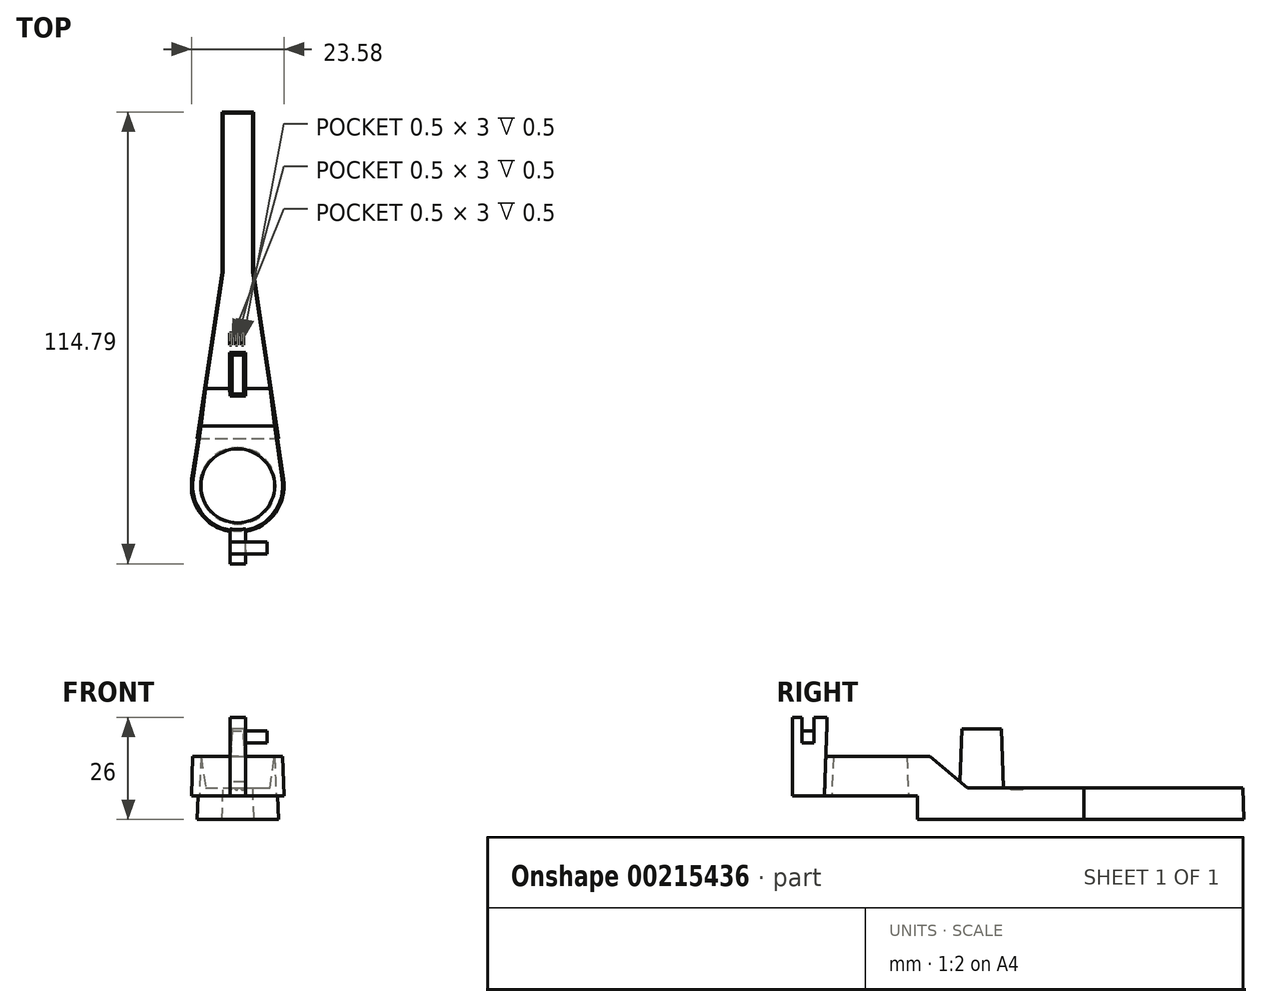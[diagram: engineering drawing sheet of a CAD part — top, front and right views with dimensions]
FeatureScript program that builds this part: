
annotation { "Feature Type Name" : "Feature", "Feature Type Description" : "" }
export const myFeature = defineFeature(function(context is Context, id is Id, definition is map)
    precondition{}
    {
        {
            var Q0;
            Q0=qCreatedBy(makeId("Top.planeOp"),FACE);
            var sketch = newSketch(context, id + "F0", { "sketchPlane" : qUnion([Q0])});
            skCircle(sketch, "E0", {"center": v(0, 0) * mm, "radius": 12 * mm});
            skLineSegment(sketch, "E1", {"start": v(-3, 95) * mm, "end": v(3, 95) * mm});
            skLineSegment(sketch, "E2", {"start": v(0, -12) * mm, "end": v(0, 95) * mm, "construction": true});
            skPoint(sketch, "E3", {"position": v(0, 95) * mm});
            skLineSegment(sketch, "E4", {"start": v(-4, 54.32) * mm, "end": v(-11.87, 1.78) * mm});
            skLineSegment(sketch, "E5", {"start": v(4, 54.32) * mm, "end": v(11.87, 1.78) * mm});
            skLineSegment(sketch, "E6", {"start": v(-3, 95) * mm, "end": v(-4, 95) * mm});
            skLineSegment(sketch, "E7", {"start": v(-4, 95) * mm, "end": v(-4, 54.32) * mm});
            skLineSegment(sketch, "E8", {"start": v(3, 95) * mm, "end": v(4, 95) * mm});
            skLineSegment(sketch, "E9", {"start": v(4, 95) * mm, "end": v(4, 54.32) * mm});
            skPoint(sketch, "E10.orphan", {"position": v(-3, 61) * mm});
            skPoint(sketch, "E11.orphan", {"position": v(3, 61) * mm});
            skSolve(sketch);
        }
        {
            var Q0;
            Q0=qSketchRegion(id+"F0",true);
            extrude(context, id + "F1", {"entities" : qUnion([Q0]), "depth" : 16 * mm, "hasDraft" : true, "draftAngle" : 2 * degree, "draftPullDirection" : true});
        }
        {
            var Q0;
            Q0=qCreatedBy(makeId("Right.planeOp"),FACE);
            cPlane(context, id + "F2", {"entities" : qUnion([Q0]), "cplaneType" : CPlaneType.OFFSET, "offset" : 12 * mm, "width" : 150 * mm, "height" : 150 * mm});
        }
        {
            var Q0;
            Q0=qCreatedBy(id+"F2.planeOp",FACE);
            var sketch = newSketch(context, id + "F3", { "sketchPlane" : qUnion([Q0])});
            skLineSegment(sketch, "E12", {"start": v(94.72, 8) * mm, "end": v(24.72, 8) * mm});
            skLineSegment(sketch, "E13", {"start": v(24.72, 8) * mm, "end": v(15.19, 16) * mm});
            skLineSegment(sketch, "E14", {"start": v(12, 0) * mm, "end": v(12, 6) * mm});
            skLineSegment(sketch, "E15", {"start": v(12, 6) * mm, "end": v(-11.8, 6) * mm});
            skLineSegment(sketch, "E16", {"start": v(12, 0) * mm, "end": v(-12, 0) * mm});
            skLineSegment(sketch, "E17", {"start": v(-12, 0) * mm, "end": v(-11.8, 6) * mm});
            skLineSegment(sketch, "E18", {"start": v(15.19, 16) * mm, "end": v(94.44, 16) * mm});
            skLineSegment(sketch, "E19", {"start": v(94.44, 16) * mm, "end": v(94.72, 8) * mm});
            skSolve(sketch);
        }
        {
            var Q0;
            Q0=qSketchRegion(id+"F3",true);
            extrude(context, id + "F4", {"entities" : qUnion([Q0]), "operationType" : NewBodyOperationType.REMOVE, "endBound" : BoundingType.THROUGH_ALL, "oppositeDirection" : true, "depth" : 25 * mm});
        }
        {
            var Q0;
            Q0=makeQuery(id+"F4.boolean.opBoolean","COPY",FACE,{"derivedFrom":makeQuery(id+"F4.opExtrude","SWEPT_FACE",FACE,{"disambiguationData":[OSD([sQuery(id+"F3.wireOp",EDGE,"E12")])]})});
            cPlane(context, id + "F5", {"entities" : qUnion([Q0]), "cplaneType" : CPlaneType.OFFSET, "offset" : 15 * mm, "width" : 150 * mm, "height" : 150 * mm});
        }
        {
            var Q0;
            Q0=qCreatedBy(id+"F5.planeOp",FACE);
            var sketch = newSketch(context, id + "F6", { "sketchPlane" : qUnion([Q0])});
            skLineSegment(sketch, "E20.bottom", {"start": v(-1.5, 23.3) * mm, "end": v(1.5, 23.3) * mm});
            skLineSegment(sketch, "E20.top", {"start": v(-1.5, 33.3) * mm, "end": v(1.5, 33.3) * mm});
            skLineSegment(sketch, "E20.left", {"start": v(-1.5, 23.3) * mm, "end": v(-1.5, 33.3) * mm});
            skLineSegment(sketch, "E20.right", {"start": v(1.5, 23.3) * mm, "end": v(1.5, 33.3) * mm});
            skPoint(sketch, "E20.middle", {"position": v(0, 28.3) * mm});
            skSolve(sketch);
        }
        {
            var Q0;
            Q0=qSketchRegion(id+"F6",true);
            extrude(context, id + "F7", {"entities" : qUnion([Q0]), "operationType" : NewBodyOperationType.ADD, "endBound" : BoundingType.UP_TO_NEXT, "oppositeDirection" : true, "depth" : 25 * mm, "hasDraft" : true, "draftAngle" : 2 * degree});
        }
        {
            var Q0;
            Q0=makeQuery(id+"F4.boolean.opBoolean","COPY",FACE,{"derivedFrom":makeQuery(id+"F4.opExtrude","SWEPT_FACE",FACE,{"disambiguationData":[OSD([sQuery(id+"F3.wireOp",EDGE,"E15")])]})});
            var sketch = newSketch(context, id + "F8", { "sketchPlane" : qUnion([Q0])});
            skCircle(sketch, "E21", {"center": v(0, 0) * mm, "radius": 9.72 * mm});
            skSolve(sketch);
        }
        {
            var Q0;
            Q0=qSketchRegion(id+"F8",true);
            extrude(context, id + "F9", {"entities" : qUnion([Q0]), "operationType" : NewBodyOperationType.REMOVE, "endBound" : BoundingType.THROUGH_ALL, "oppositeDirection" : true, "depth" : 25 * mm, "hasDraft" : true, "draftAngle" : 2 * degree, "draftPullDirection" : true});
        }
        {
            var Q0;
            Q0=makeQuery(id+"F4.boolean.opBoolean","COPY",FACE,{"derivedFrom":makeQuery(id+"F4.opExtrude","SWEPT_FACE",FACE,{"disambiguationData":[OSD([sQuery(id+"F3.wireOp",EDGE,"E15")])]})});
            var sketch = newSketch(context, id + "F10", { "sketchPlane" : qUnion([Q0])});
            skLineSegment(sketch, "E22", {"start": v(0, 11.8) * mm, "end": v(0, 19.8) * mm, "construction": true});
            skPoint(sketch, "E22.endSnap0", {"position": v(0, 11.8) * mm});
            skLineSegment(sketch, "E23", {"start": v(0, 19.8) * mm, "end": v(-2, 19.8) * mm});
            skLineSegment(sketch, "E24", {"start": v(-2, 19.8) * mm, "end": v(-2, 11.62) * mm});
            skLineSegment(sketch, "E25", {"start": v(0, 19.8) * mm, "end": v(2, 19.8) * mm});
            skLineSegment(sketch, "E26", {"start": v(2, 19.8) * mm, "end": v(2, 11.62) * mm});
            skArc(sketch, "E27", {"start": v(2, 11.62) * mm, "mid": v(0, 11.8) * mm, "end": v(-2, 11.62) * mm});
            skSolve(sketch);
        }
        {
            var Q0;
            Q0=qCreatedBy(makeId("Front.planeOp"),FACE);
            var Q1;
            Q1=sQuery(id+"F10.wireOp",VERTEX,"E25.start");
            cPlane(context, id + "F11", {"entities" : qUnion([Q0, Q1]), "cplaneType" : CPlaneType.PLANE_POINT, "offset" : 25 * mm, "width" : 150 * mm, "height" : 150 * mm});
        }
        {
            var Q0;
            Q0=qCreatedBy(id+"F11.planeOp",FACE);
            var sketch = newSketch(context, id + "F12", { "sketchPlane" : qUnion([Q0])});
            skLineSegment(sketch, "E28.bottom", {"start": v(-2, 6) * mm, "end": v(2, 6) * mm});
            skLineSegment(sketch, "E28.top", {"start": v(-2, 26) * mm, "end": v(2, 26) * mm});
            skLineSegment(sketch, "E28.left", {"start": v(-2, 6) * mm, "end": v(-2, 26) * mm});
            skLineSegment(sketch, "E28.right", {"start": v(2, 6) * mm, "end": v(2, 26) * mm});
            skSolve(sketch);
        }
        {
            var Q0;
            Q0=qSketchRegion(id+"F12",true);
            var Q1;
            Q1=makeQuery(id+"F1.opExtrude","SWEPT_FACE",FACE,{"disambiguationData":[OSD([sQuery(id+"F0.wireOp",EDGE,"E0")])]});
            extrude(context, id + "F13", {"entities" : qUnion([Q0]), "operationType" : NewBodyOperationType.ADD, "endBound" : BoundingType.UP_TO_SURFACE, "oppositeDirection" : true, "endBoundEntityFace" : qUnion([Q1]), "depth" : 8 * mm});
        }
        {
            var Q0;
            Q0=makeQuery(id+"F13.opExtrude","SWEPT_FACE",FACE,{"disambiguationData":[OSD([sQuery(id+"F12.wireOp",EDGE,"E28.right")])]});
            var sketch = newSketch(context, id + "F14", { "sketchPlane" : qUnion([Q0])});
            skLineSegment(sketch, "E29.bottom", {"start": v(-17.3, 22.5) * mm, "end": v(-14.3, 22.5) * mm});
            skLineSegment(sketch, "E29.top", {"start": v(-17.3, 19.5) * mm, "end": v(-14.3, 19.5) * mm});
            skLineSegment(sketch, "E29.left", {"start": v(-17.3, 22.5) * mm, "end": v(-17.3, 19.5) * mm});
            skLineSegment(sketch, "E29.right", {"start": v(-14.3, 22.5) * mm, "end": v(-14.3, 19.5) * mm});
            skSolve(sketch);
        }
        {
            var Q0;
            Q0=qSketchRegion(id+"F14",true);
            extrude(context, id + "F15", {"entities" : qUnion([Q0]), "operationType" : NewBodyOperationType.ADD, "depth" : 5.5 * mm});
        }
        {
            var Q0;
            Q0=makeQuery(id+"F13.opExtrude","SWEPT_FACE",FACE,{"disambiguationData":[OSD([sQuery(id+"F12.wireOp",EDGE,"E28.right")])]});
            var sketch = newSketch(context, id + "F16", { "sketchPlane" : qUnion([Q0])});
            skLineSegment(sketch, "E30.bottom", {"start": v(-17.3, 22.5) * mm, "end": v(-14.3, 22.5) * mm});
            skLineSegment(sketch, "E30.top", {"start": v(-17.3, 26) * mm, "end": v(-14.3, 26) * mm});
            skLineSegment(sketch, "E30.left", {"start": v(-17.3, 22.5) * mm, "end": v(-17.3, 26) * mm});
            skLineSegment(sketch, "E30.right", {"start": v(-14.3, 22.5) * mm, "end": v(-14.3, 26) * mm});
            skSolve(sketch);
        }
        {
            var Q0;
            Q0=qSketchRegion(id+"F16",true);
            extrude(context, id + "F17", {"entities" : qUnion([Q0]), "operationType" : NewBodyOperationType.REMOVE, "endBound" : BoundingType.THROUGH_ALL, "oppositeDirection" : true, "depth" : 25 * mm});
        }
        {
            var Q0;
            Q0=makeQuery(id+"F4.boolean.opBoolean","COPY",FACE,{"derivedFrom":makeQuery(id+"F4.opExtrude","SWEPT_FACE",FACE,{"disambiguationData":[OSD([sQuery(id+"F3.wireOp",EDGE,"E12")])]})});
            var sketch = newSketch(context, id + "F18", { "sketchPlane" : qUnion([Q0])});
            skLineSegment(sketch, "E31.bottom", {"start": v(-2.02, 38.82) * mm, "end": v(1.48, 38.82) * mm});
            skLineSegment(sketch, "E31.top", {"start": v(-2.02, 35.82) * mm, "end": v(1.48, 35.82) * mm});
            skLineSegment(sketch, "E31.left", {"start": v(-2.02, 38.82) * mm, "end": v(-2.02, 35.82) * mm});
            skLineSegment(sketch, "E31.right", {"start": v(1.48, 38.82) * mm, "end": v(1.48, 35.82) * mm});
            skLineSegment(sketch, "E32", {"start": v(-1.52, 38.82) * mm, "end": v(-1.52, 35.82) * mm});
            skLineSegment(sketch, "E33", {"start": v(-0.5, 38.82) * mm, "end": v(-0.5, 35.82) * mm});
            skLineSegment(sketch, "E34", {"start": v(0, 38.82) * mm, "end": v(0, 35.82) * mm});
            skLineSegment(sketch, "E35", {"start": v(0.98, 38.82) * mm, "end": v(0.98, 35.82) * mm});
            skSolve(sketch);
        }
        {
            var Q0;
            {var subQ0=sQuery(id+"F18.wireOp",EDGE,"E31.left");Q0=makeQuery(id+"F18.imprint","IMPRINT",FACE,{"disambiguationData":[TD([[makeQuery(id+"F18.imprint","IMPRINT",EDGE,{"derivedFrom":subQ0}),1.0]])]});}
            var Q1;
            {var subQ0=sQuery(id+"F18.wireOp",EDGE,"E33");Q1=makeQuery(id+"F18.imprint","IMPRINT",FACE,{"disambiguationData":[TD([[makeQuery(id+"F18.imprint","IMPRINT",EDGE,{"derivedFrom":subQ0}),1.0]])]});}
            var Q2;
            {var subQ0=sQuery(id+"F18.wireOp",EDGE,"E31.right");Q2=makeQuery(id+"F18.imprint","IMPRINT",FACE,{"disambiguationData":[TD([[makeQuery(id+"F18.imprint","IMPRINT",EDGE,{"derivedFrom":subQ0}),-1.0]])]});}
            extrude(context, id + "F19", {"entities" : qUnion([Q0, Q1, Q2]), "operationType" : NewBodyOperationType.REMOVE, "oppositeDirection" : true, "depth" : 0.5 * mm});
        }
    });
